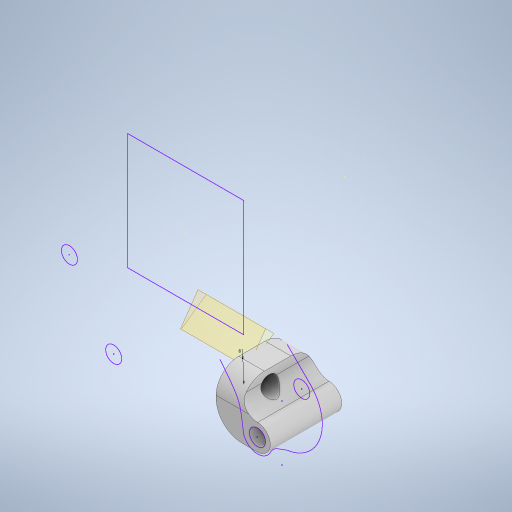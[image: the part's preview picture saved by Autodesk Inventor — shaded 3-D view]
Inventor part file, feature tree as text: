
AUTODESK INVENTOR PART (.ipt)
format: ipt  version: 2023 (Build 270158000, 158)  size: 746,496 bytes
history: native  units: in
note: dims shown in document units (in); Inventor stores cm internally (conversion verified against a paired STEP export)
features: other x26, sketch x8, projected_geometry x7, extrude x6, fillet x5, plane x3, chamfer x1
ambient origin geometry x8: Origin, YZ Plane, XZ Plane, XY Plane, X Axis, Y Axis, Z Axis, Center Point
bodies: Solid1 (feature_tree)
feature tree (56):
  other  "pre camera mount assem.iam"
  other  "NightStickmax full assem.iam:1::bottom plate NightStickmax.ipt:1"
  other  "NightStickmax full assem.iam:1::arm stack.iam:1::arm NightStickmax.ipt:1"
  other  "NightStickmax full assem.iam:1::arm stack.iam:1::arm NightStickmax.ipt:2"
  other  "NightStickmax full assem.iam:1::arm stack.iam:2::arm NightStickmax.ipt:1"
  other  "NightStickmax full assem.iam:1::arm stack.iam:2::arm NightStickmax.ipt:2"
  other  "NightStickmax full assem.iam:1::arm stack.iam:3::arm NightStickmax.ipt:1"
  other  "NightStickmax full assem.iam:1::arm stack.iam:3::arm NightStickmax.ipt:2"
  other  "NightStickmax full assem.iam:1::arm stack.iam:4::arm NightStickmax.ipt:1"
  other  "NightStickmax full assem.iam:1::arm stack.iam:4::arm NightStickmax.ipt:2"
  other  "NightStickmax full assem.iam:1::mid plate NightStickmax.ipt:1"
  other  "NightStickmax full assem.iam:1::25mm standoff.ipt:1"
  other  "NightStickmax full assem.iam:1::25mm standoff.ipt:2"
  other  "NightStickmax full assem.iam:1::25mm standoff.ipt:3"
  other  "NightStickmax full assem.iam:1::25mm standoff.ipt:4"
  other  "NightStickmax full assem.iam:1::25mm standoff.ipt:5"
  other  "NightStickmax full assem.iam:1::25mm standoff.ipt:6"
  other  "NightStickmax full assem.iam:1::25mm standoff.ipt:7"
  other  "NightStickmax full assem.iam:1::25mm standoff.ipt:8"
  other  "NightStickmax full assem.iam:1::30x30 stack.ipt:1"
  other  "NightStickmax full assem.iam:1::4700uF cap.ipt:1"
  other  "NightStickmax full assem.iam:1::4700uF cap holder.ipt:1"
  other  "NightStickmax full assem.iam:1::HDzero micro dummy.ipt:1"
  other  "NightStickmax full assem.iam:1::HDzero micro dummy.ipt:2"
  other  "NightStickmax full assem.iam:1::SMA whip holder.ipt:1"
  other  "pre camera mount block.ipt:1"
  extrude  "Extrusion1"  TaperAngle=0.0deg  [1 undecoded]
  extrude  "Extrusion2"  TaperAngle=0.0deg  [1 undecoded]
  extrude  "Extrusion3"  Depth=0.2165in
  plane  "Work Plane3"
  extrude  "Extrusion4"  Depth=0.874in TaperAngle=0.0deg
  extrude  "Extrusion5"  Depth=0.4724in TaperAngle=45.0deg
  sketch  "Sketch18"  dims[d17=0.315in]
  chamfer  "Chamfer1"  Distance=0.315in
  fillet  "Fillet1"  Radius=0.1969in
  fillet  "Fillet2"  Radius=0.1969in
  extrude  "Extrusion6"  Depth=0.1969in
  sketch  "Sketch20"  dims[d23=0.315in d24=0.315in d25=0.1969in d26=0.1969in d28=0.315in d29=0.0in d30=0.0in d31=0.2756in d32=0.2756in d33=0.1969in]
  fillet  "Fillet4"  [1 undecoded]
  fillet  "Fillet5"  Radius=0.2756in
  fillet  "Fillet6"  Radius=0.2756in
  plane  "Work Plane1"
  plane  "Work Plane1_1"
  sketch  "Sketch13"  dims[d0=0.3937in d1=0.0in d2=0.0in]
  projected_geometry  "Projected Loop1"
  sketch  "Sketch14"  dims[d3=0.0in d4=0.0in d5=0.0in d6=0.0in]
  projected_geometry  "Projected Loop2"
  projected_geometry  "Projected Loop3"
  sketch  "Sketch15"  dims[d7=-0.1181in d8=0.2165in]
  projected_geometry  "Projected Loop4"
  sketch  "Sketch16"  dims[d9=0.0in d10=0.0in d11=0.874in d12=0.0in]
  sketch  "Sketch17"  dims[d13=0.315in d14=0.4724in d15=0.0787in d16=45.0deg]
  projected_geometry  "Projected Loop5"
  sketch  "Sketch19"  dims[d18=1.1811in]
  projected_geometry  "Projected Loop6"
  projected_geometry  "Projected Loop7"
note: 3 required parameter values undecoded (feature->parameter linkage not recoverable at this tier; creation-order binding heuristic only, values carry confidence <= 0.55)
